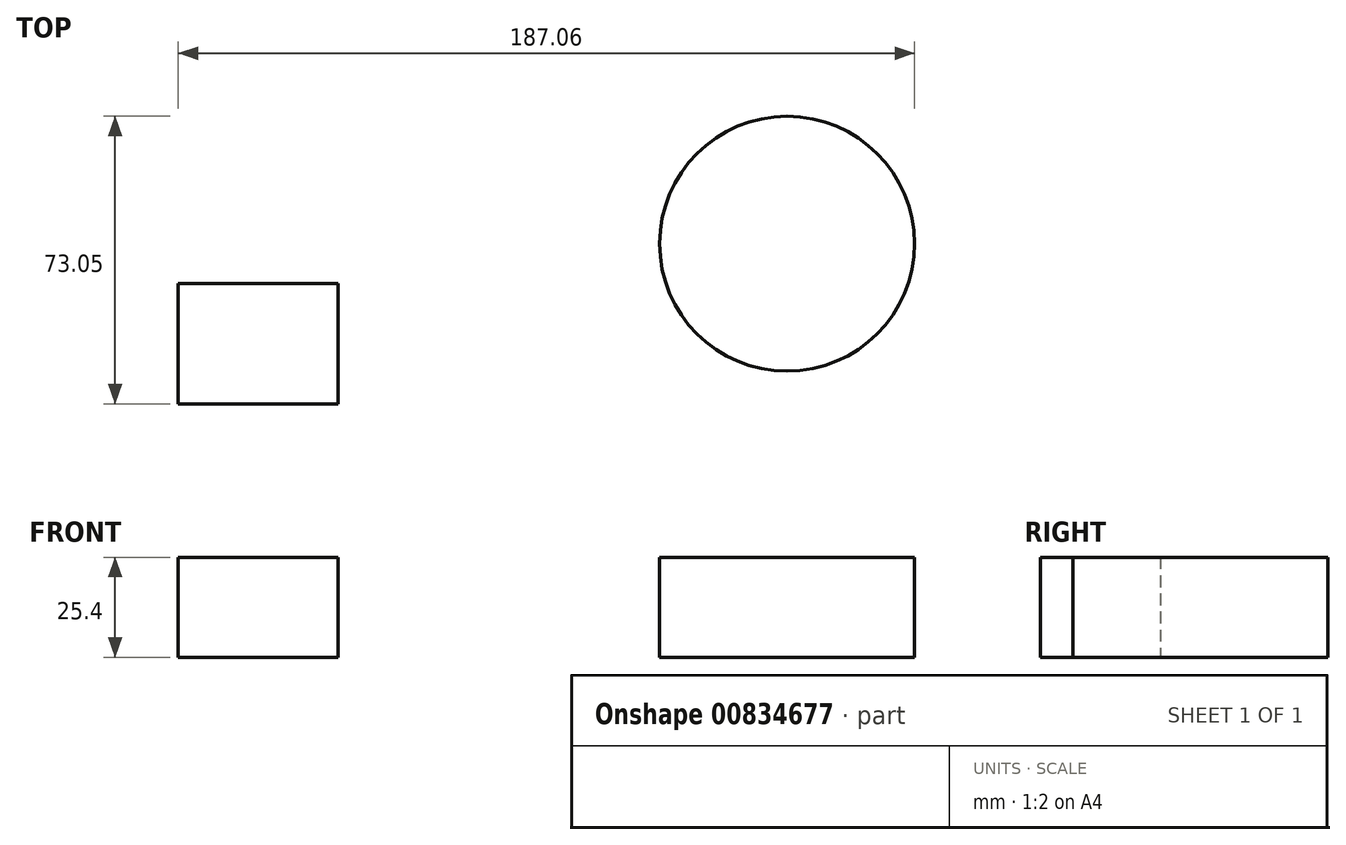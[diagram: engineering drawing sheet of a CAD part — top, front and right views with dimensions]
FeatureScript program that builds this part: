
annotation { "Feature Type Name" : "Feature", "Feature Type Description" : "" }
export const myFeature = defineFeature(function(context is Context, id is Id, definition is map)
    precondition{}
    {
        {
            var Q0;
            Q0=qCreatedBy(makeId("Top.planeOp"),FACE);
            var sketch = newSketch(context, id + "F0", { "sketchPlane" : qUnion([Q0])});
            skCircle(sketch, "E0", {"center": v(0, 0) * mm, "radius": 32.38 * mm});
            skLineSegment(sketch, "E1.bottom", {"start": v(-154.68, -10.17) * mm, "end": v(-114.02, -10.17) * mm});
            skLineSegment(sketch, "E1.top", {"start": v(-154.68, -40.67) * mm, "end": v(-114.02, -40.67) * mm});
            skLineSegment(sketch, "E1.left", {"start": v(-154.68, -10.17) * mm, "end": v(-154.68, -40.67) * mm});
            skLineSegment(sketch, "E1.right", {"start": v(-114.02, -10.17) * mm, "end": v(-114.02, -40.67) * mm});
            skSolve(sketch);
        }
        {
            var Q0;
            Q0 = qSketchRegion(id + "F0", true);
            extrude(context, id + "F1", {"entities" : qUnion([Q0]), "depth" : 25.4 * mm, "offsetDistance" : 25.4 * mm});
        }
        {
            var Q0;
            Q0 = qSketchRegion(id + "F0", true);
            extrude(context, id + "F2", {"entities" : qUnion([Q0]), "depth" : 25.4 * mm, "offsetDistance" : 25.4 * mm});
        }
    });
